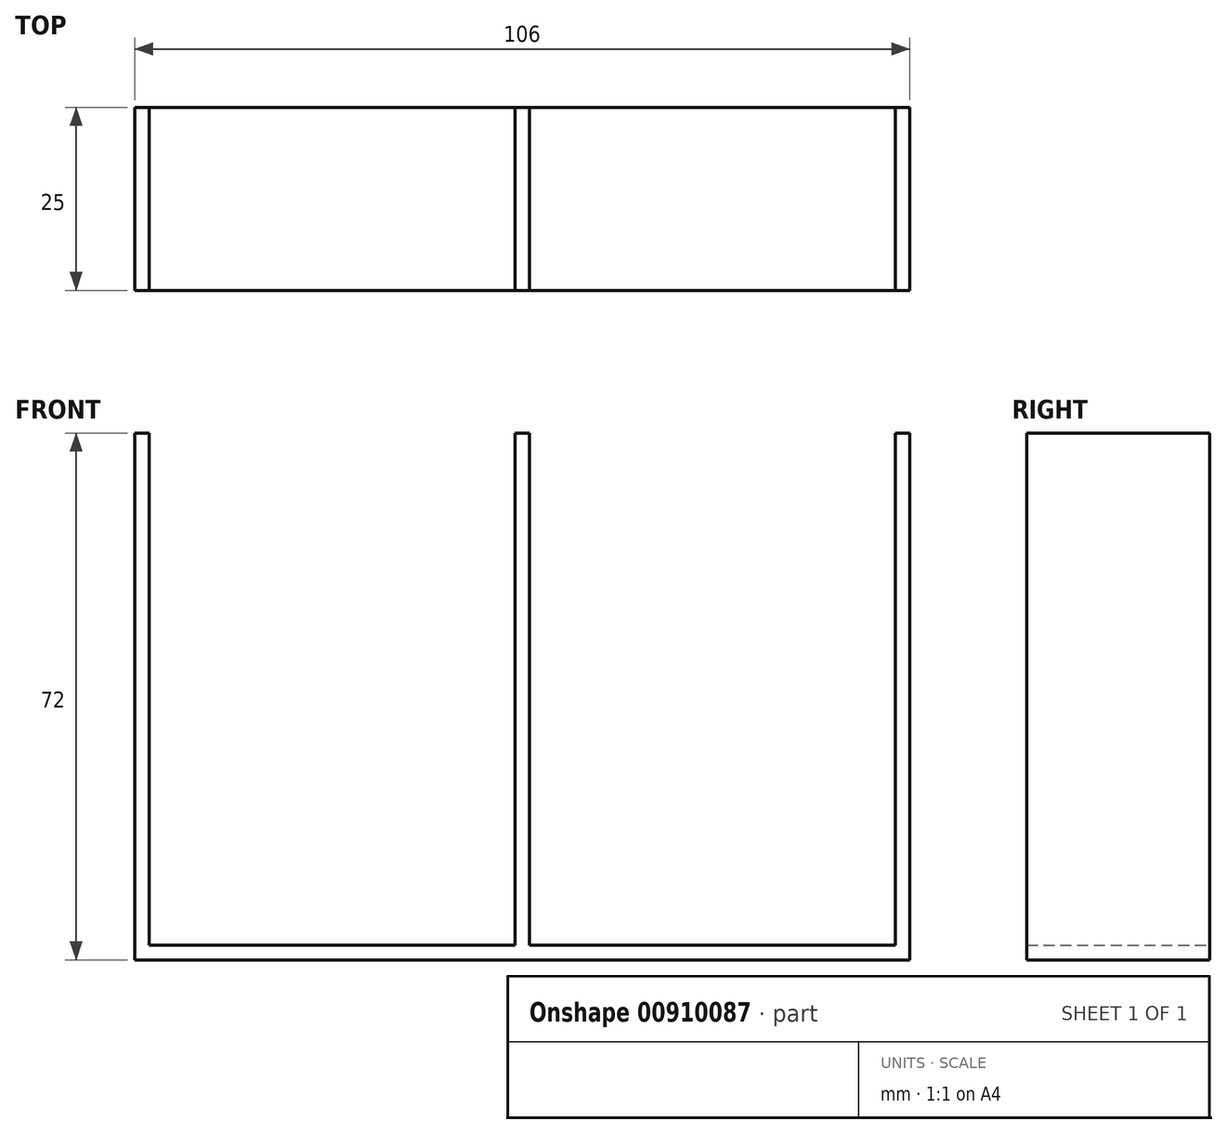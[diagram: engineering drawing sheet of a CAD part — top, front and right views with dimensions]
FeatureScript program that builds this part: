
annotation { "Feature Type Name" : "Feature", "Feature Type Description" : "" }
export const myFeature = defineFeature(function(context is Context, id is Id, definition is map)
    precondition{}
    {
        {
            var Q0;
            Q0=qCreatedBy(makeId("Front.planeOp"),FACE);
            var sketch = newSketch(context, id + "F0", { "sketchPlane" : qUnion([Q0])});
            skLineSegment(sketch, "E0", {"start": v(-127.98, 0) * mm, "end": v(-21.98, 0) * mm});
            skLineSegment(sketch, "E1", {"start": v(-21.98, 0) * mm, "end": v(-21.98, 72) * mm});
            skLineSegment(sketch, "E2", {"start": v(-21.98, 72) * mm, "end": v(-23.98, 72) * mm});
            skLineSegment(sketch, "E3", {"start": v(-23.98, 72) * mm, "end": v(-23.98, 2) * mm});
            skLineSegment(sketch, "E4", {"start": v(-21.98, 2) * mm, "end": v(-73.98, 2) * mm});
            skLineSegment(sketch, "E5", {"start": v(-73.98, 2) * mm, "end": v(-73.98, 72) * mm});
            skLineSegment(sketch, "E6", {"start": v(-73.98, 72) * mm, "end": v(-75.98, 72) * mm});
            skLineSegment(sketch, "E7", {"start": v(-75.98, 72) * mm, "end": v(-75.98, 2) * mm});
            skLineSegment(sketch, "E8", {"start": v(-75.98, 2) * mm, "end": v(-125.98, 2) * mm});
            skLineSegment(sketch, "E9", {"start": v(-125.98, 2) * mm, "end": v(-125.98, 72) * mm});
            skLineSegment(sketch, "E10", {"start": v(-125.98, 72) * mm, "end": v(-127.98, 72) * mm});
            skLineSegment(sketch, "E11", {"start": v(-127.98, 72) * mm, "end": v(-127.98, 0) * mm});
            skSolve(sketch);
        }
        {
            var Q0;
            Q0 = qSketchRegion(id + "F0", true);
            extrude(context, id + "F1", {"entities" : qUnion([Q0]), "depth" : 25 * mm, "offsetDistance" : 25 * mm});
        }
    });
